# Revit family: Doors-Sliding_WON-DOOR_Fireguard-MFW-Curved_TEST
name_source: partatom
category: Doors
units: mm (PartAtom-declared; Revit-internal decimal feet)

## family parameters
Always vertical = No
Cut with Voids When Loaded = Yes
OmniClass Number = 23.17.11.31
OmniClass Title = Fire Doors
Room Calculation Point = No
Shared = No
Work Plane-Based = Yes

## types (2) — shared parameters
Analytic Construction = <None>
Default Elevation = 4' - 0"
Define Thermal Properties by = Schematic Type
Description = The Won-Door FireGuard MFW (Movable fire wall) product is U.L. Certified as meeting the criteria required by ANSI/UL263 (ASTM E119). When the building code restricts the size of openings in a Fire Barrier, the FireGuard MFW provides a viable solution. The FireGuard MFW is available in the following U.L. ratings: MFWI (1-hour) or MFWII (2-hour).
Door Finish = Won-Door-Metal-Platinum
Half Thickness = 1' - 0"
Lookup Table = Doors-Sliding_WON-DOOR_Fireguard-MFW-Curved
Manufacturer = Won-Door Corporation
Model = Fireguard MFW Curved
Product Page URL = https://wondoor.com
Product data url = https://www.bimobject.com
Sweep Thickness = 2' - 0"
Thickness = 2' - 0"
URL = https://www.wondoor.com
Version = 1

## per-type parameters (varying)
| type | Fire Rating | Pocket Thickness |
| 120 Minute | 120 Minute Fire Rating | 3' - 0 1/4" |
| 60 Minute | 60 Minute Fire Rating | 2' - 9 3/4" |

## geometry (parser evidence)
native form markers: Sweep x25
no freeform markers — native parametric forms only
